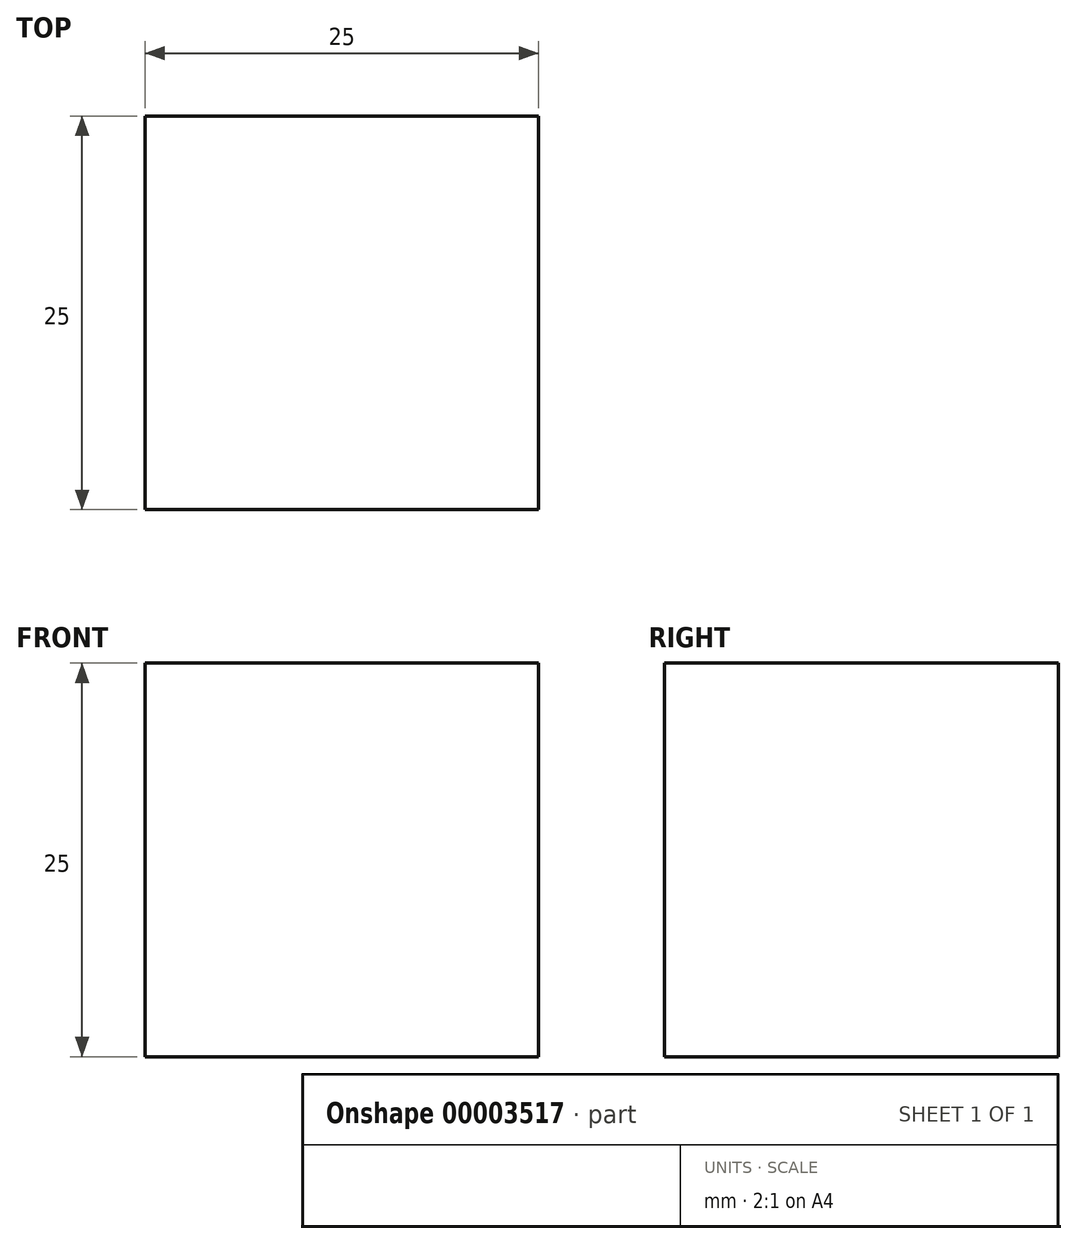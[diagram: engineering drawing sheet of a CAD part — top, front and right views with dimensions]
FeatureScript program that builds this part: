
annotation { "Feature Type Name" : "Feature", "Feature Type Description" : "" }
export const myFeature = defineFeature(function(context is Context, id is Id, definition is map)
    precondition{}
    {
        {
            var Q0;
            Q0=qCreatedBy(makeId("Top.planeOp"),FACE);
            var sketch = newSketch(context, id + "F0", { "sketchPlane" : qUnion([Q0])});
            skLineSegment(sketch, "E0.rect.bottom", {"start": v(12.5, -12.5) * mm, "end": v(-12.5, -12.5) * mm});
            skLineSegment(sketch, "E0.rect.top", {"start": v(12.5, 12.5) * mm, "end": v(-12.5, 12.5) * mm});
            skLineSegment(sketch, "E0.rect.left", {"start": v(12.5, -12.5) * mm, "end": v(12.5, 12.5) * mm});
            skLineSegment(sketch, "E0.rect.right", {"start": v(-12.5, -12.5) * mm, "end": v(-12.5, 12.5) * mm});
            skPoint(sketch, "E0.rect.middle", {"position": v(0, 0) * mm});
            skSolve(sketch);
        }
        {
            var Q0;
            Q0 = qSketchRegion(id + "F0", true);
            extrude(context, id + "F1", {"entities" : qUnion([Q0]), "depth" : 25 * mm});
        }
    });
